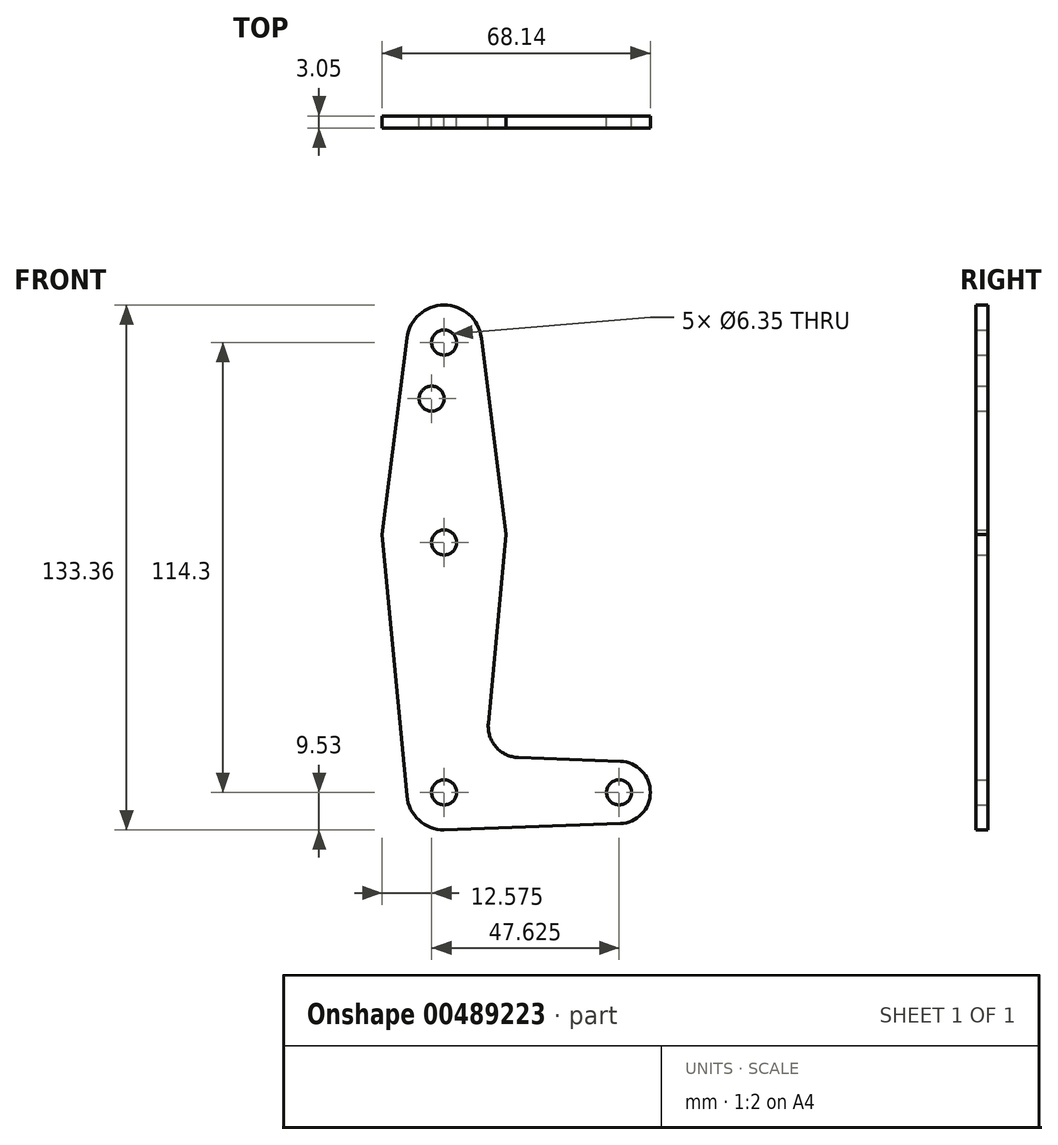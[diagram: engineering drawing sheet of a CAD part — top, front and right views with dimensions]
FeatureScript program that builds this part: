
annotation { "Feature Type Name" : "Feature", "Feature Type Description" : "" }
export const myFeature = defineFeature(function(context is Context, id is Id, definition is map)
    precondition{}
    {
        {
            var Q0;
            Q0=qCreatedBy(makeId("Front.planeOp"),FACE);
            var sketch = newSketch(context, id + "F0", { "sketchPlane" : qUnion([Q0])});
            skLineSegment(sketch, "E0", {"start": v(0, 0) * mm, "end": v(0, 114.3) * mm, "construction": true});
            skLineSegment(sketch, "E1", {"start": v(0, 114.3) * mm, "end": v(0, 0) * mm, "construction": true});
            skLineSegment(sketch, "E2", {"start": v(0, 0) * mm, "end": v(44.45, 0) * mm, "construction": true});
            skCircle(sketch, "E3", {"center": v(0, 0) * mm, "radius": 9.53 * mm});
            skCircle(sketch, "E4", {"center": v(0, 114.3) * mm, "radius": 9.53 * mm});
            skCircle(sketch, "E5", {"center": v(0, 63.5) * mm, "radius": 15.88 * mm});
            skCircle(sketch, "E6", {"center": v(44.45, 0) * mm, "radius": 7.94 * mm});
            skLineSegment(sketch, "E7", {"start": v(0, 63.5) * mm, "end": v(0, 0) * mm, "construction": true});
            skLineSegment(sketch, "E8", {"start": v(9.45, 115.5) * mm, "end": v(15.75, 65.48) * mm});
            skLineSegment(sketch, "E9", {"start": v(15.75, 65.48) * mm, "end": v(11.22, 17.55) * mm});
            skLineSegment(sketch, "E10", {"start": v(-9.45, 115.5) * mm, "end": v(-15.75, 65.48) * mm});
            skLineSegment(sketch, "E11", {"start": v(-15.75, 65.48) * mm, "end": v(-9.48, -0.9) * mm});
            skLineSegment(sketch, "E12", {"start": v(18.86, 8.85) * mm, "end": v(44.73, 7.93) * mm});
            skLineSegment(sketch, "E13", {"start": v(0, -9.53) * mm, "end": v(44.73, -7.93) * mm});
            skCircle(sketch, "E14", {"center": v(0, 114.3) * mm, "radius": 3.18 * mm});
            skCircle(sketch, "E15", {"center": v(0, 63.5) * mm, "radius": 3.18 * mm});
            skCircle(sketch, "E16", {"center": v(0, 0) * mm, "radius": 3.18 * mm});
            skCircle(sketch, "E17", {"center": v(44.45, 0) * mm, "radius": 3.18 * mm});
            skLineSegment(sketch, "E18", {"start": v(0, 63.5) * mm, "end": v(0, 100.03) * mm, "construction": true});
            skLineSegment(sketch, "E19", {"start": v(0, 100.03) * mm, "end": v(-3.18, 100.03) * mm, "construction": true});
            skCircle(sketch, "E20", {"center": v(-3.18, 100.03) * mm, "radius": 3.18 * mm});
            skPoint(sketch, "E21.newPointB", {"position": v(0, 9.53) * mm});
            skArc(sketch, "E21.filletArc", {"start": v(11.22, 17.55) * mm, "mid": v(13.16, 11.55) * mm, "end": v(18.86, 8.85) * mm});
            skSolve(sketch);
        }
        {
            var Q0;
            {var subQ0=sQuery(id+"F0.wireOp",EDGE,"E8");Q0=makeQuery(id+"F0.imprint","IMPRINT",FACE,{"disambiguationData":[TD([[makeQuery(id+"F0.imprint","IMPRINT",EDGE,{"derivedFrom":subQ0}),-1.0]])]});}
            var Q1;
            Q1=makeQuery(id+"F0.imprint","IMPRINT",FACE,{"disambiguationData":[TD([[makeQuery(id+"F0.imprint","IMPRINT",EDGE,{"derivedFrom":sQuery(id+"F0.wireOp",EDGE,"E14")}),-1.0]])]});
            var Q2;
            Q2=makeQuery(id+"F0.imprint","IMPRINT",FACE,{"disambiguationData":[TD([[makeQuery(id+"F0.imprint","IMPRINT",EDGE,{"derivedFrom":sQuery(id+"F0.wireOp",EDGE,"E15")}),-1.0]])]});
            var Q3;
            {var subQ9=sQuery(id+"F0.wireOp",EDGE,"E12");Q3=makeQuery(id+"F0.imprint","IMPRINT",FACE,{"disambiguationData":[TD([[makeQuery(id+"F0.imprint","IMPRINT",EDGE,{"derivedFrom":subQ9}),-1.0]])]});}
            var Q4;
            Q4=makeQuery(id+"F0.imprint","IMPRINT",FACE,{"disambiguationData":[TD([[makeQuery(id+"F0.imprint","IMPRINT",EDGE,{"derivedFrom":sQuery(id+"F0.wireOp",EDGE,"E16")}),-1.0]])]});
            var Q5;
            Q5=makeQuery(id+"F0.imprint","IMPRINT",FACE,{"disambiguationData":[TD([[makeQuery(id+"F0.imprint","IMPRINT",EDGE,{"derivedFrom":sQuery(id+"F0.wireOp",EDGE,"E17")}),-1.0]])]});
            extrude(context, id + "F1", {"entities" : qUnion([Q0, Q1, Q2, Q3, Q4, Q5]), "depth" : 3.05 * mm});
        }
    });
